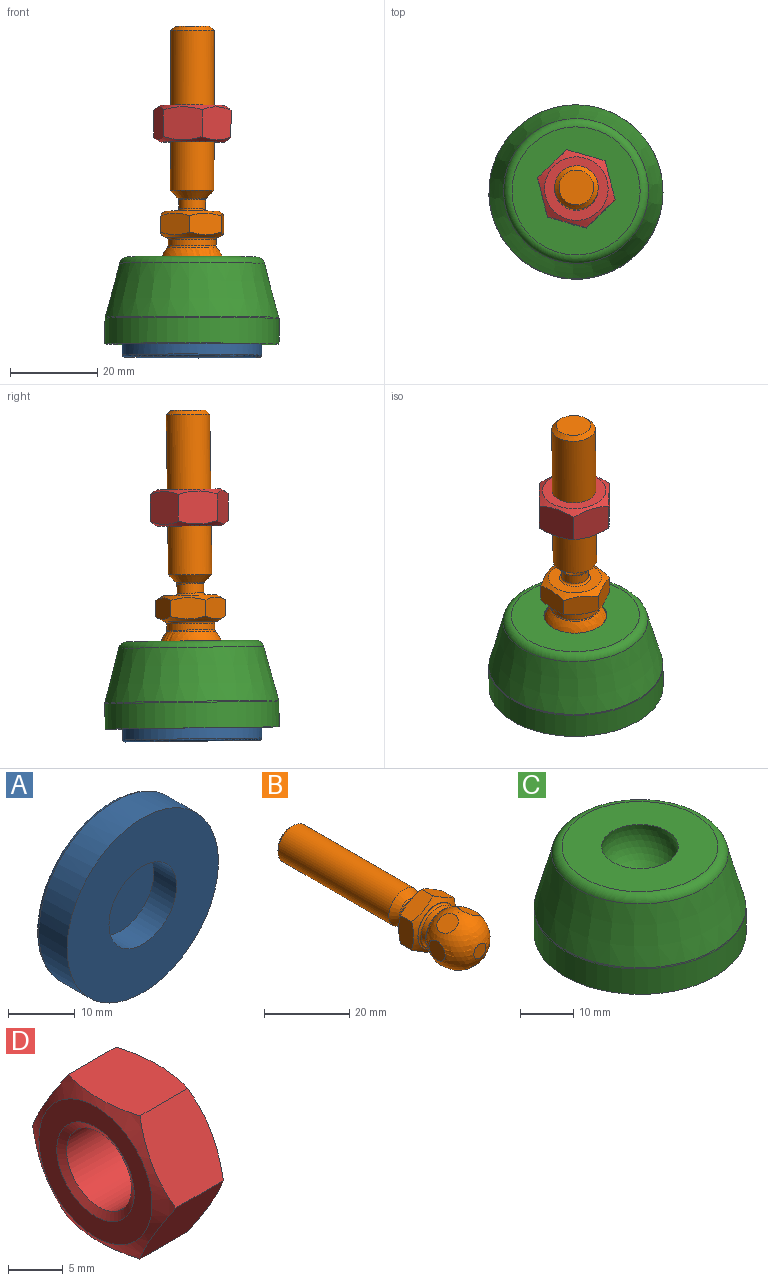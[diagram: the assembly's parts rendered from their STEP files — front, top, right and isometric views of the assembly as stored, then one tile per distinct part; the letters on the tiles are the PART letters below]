
ASSEMBLY  parts=4 mates=3
PART A: 6 faces, bbox 34.6x6.5x34.6 mm
  f0: torus R=15.5mm, axis (0,1,0), area 78.1mm2, adj f1,f2
  f1: plane 31x31mm, normal (0,1,0), area 754.8mm2, adj f0
  f2: cylinder r=16mm len=32mm, axis (0,1,0), area 603.2mm2, adj f0,f5
  f3: plane 14.3x14.3mm, normal (0,-1,0), area 160.6mm2, adj f4
  f4: cylinder r=7.15mm len=14.3mm, axis (0,1,0), area 215.6mm2, adj f3,f5
  f5: plane 32x32mm, normal (0,-1,0), area 643.6mm2, adj f2,f4
PART B: 28 faces, bbox 16.2x63.3x16.2 mm
  f0: torus R=3.56mm, axis (0,-1,0), area 16mm2, adj f1,f2
  f1: cylinder r=3.06mm len=6.12mm, axis (0,1,0), area 40.2mm2, adj f0,f3
  f2: plane 12.17x12.17mm, normal (0,1,0), area 76.4mm2, adj f0,f11
  f3: torus R=3.56mm, axis (0,1,0), area 7.7mm2, adj f1,f4
  f4: cone r=4.03mm half-angle=45deg, axis (0,1,0), area 65.4mm2, adj f3,f16
  f5: torus R=6mm, axis (0,1,0), area 12.6mm2, adj f6,f7
  f6: cylinder r=5.5mm len=11mm, axis (0,1,0), area 51.1mm2, adj f5,f8
  f7: sphere r=7.5mm, area 433mm2, adj f5,f18,f19,f20,f21,f22,f23,f27
  f8: torus R=6mm, axis (0,1,0), area 28mm2, adj f6,f9
  f9: plane 12.17x12.17mm, normal (0,-1,0), area 3.1mm2, adj f8,f10
  f10: cone r=7.08mm half-angle=60deg, axis (0,1,0), area 61.8mm2, adj f9,f12,f13,f14,f24,f25,f26
  f11: cone r=7.08mm half-angle=60deg, axis (0,-1,0), area 61.8mm2, adj f2,f12,f13,f14,f24,f25,f26
  f12: plane 7x5.54mm, normal (-0.5,0,-0.87), area 36.5mm2, adj f10,f11,f13,f25
  f13: plane 8.08x5.54mm, normal (-1,0,0), area 36.5mm2, adj f10,f11,f12,f14
  f14: plane 7x5.54mm, normal (-0.5,0,0.87), area 36.5mm2, adj f10,f11,f13,f24
  f15: cone r=4.5mm half-angle=45deg, axis (0,-1,0), area 40mm2, adj f16,f17
  f16: cylinder r=5mm len=36.76mm, axis (0,1,0), area 1154.8mm2, adj f4,f15
  f17: plane 8x8mm, normal (0,1,0), area 50.3mm2, adj f15
  f18: plane 5.39x5.39mm, normal (-1,0,0), area 22.8mm2, adj f7
  f19: plane 5.39x4.66mm, normal (-0.5,0,-0.87), area 22.8mm2, adj f7
  f20: plane 5.39x4.66mm, normal (0.5,0,-0.87), area 22.8mm2, adj f7
  f21: plane 5.39x5.39mm, normal (1,0,0), area 22.8mm2, adj f7
  f22: plane 5.39x4.66mm, normal (0.5,0,0.87), area 22.8mm2, adj f7
  f23: plane 5.39x4.66mm, normal (-0.5,0,0.87), area 22.8mm2, adj f7
  f24: plane 7x5.54mm, normal (0.5,0,0.87), area 36.5mm2, adj f10,f11,f14,f26
  f25: plane 7x5.54mm, normal (0.5,0,-0.87), area 36.5mm2, adj f10,f11,f12,f26
  f26: plane 8.08x5.54mm, normal (1,0,0), area 36.5mm2, adj f10,f11,f24,f25
  f27: plane 4x4mm, normal (0,-1,0), area 12.6mm2, adj f7
PART C: 58 faces, bbox 43.3x43.3x20 mm
  f0: plane 9x6.43mm, normal (0.71,-0.71,0), area 69.3mm2, adj f2,f27,f35,f43,f45,f56
  f1: plane 9x6.43mm, normal (-0.71,0.71,0), area 69.3mm2, adj f2,f28,f36,f44,f45,f56
  f2: plane 8.55x8.55mm, normal (0,0,-1), area 27.1mm2, adj f0,f1,f45,f56
  f3: plane 9.09x9mm, normal (0,-1,0), area 69.3mm2, adj f5,f28,f36,f44,f45,f56
  f4: plane 9.09x9mm, normal (0,1,0), area 69.3mm2, adj f5,f26,f34,f42,f45,f56
  f5: plane 9.16x3mm, normal (0,0,-1), area 27.1mm2, adj f3,f4,f45,f56
  f6: plane 9x6.43mm, normal (-0.71,-0.71,0), area 69.3mm2, adj f8,f26,f34,f42,f45,f56
  f7: plane 9x6.43mm, normal (0.71,0.71,0), area 69.3mm2, adj f8,f25,f33,f41,f45,f56
  f8: plane 8.55x8.55mm, normal (0,0,-1), area 27.1mm2, adj f6,f7,f45,f56
  f9: plane 9.09x9mm, normal (-1,0,0), area 69.3mm2, adj f11,f25,f33,f41,f45,f56
  f10: plane 9.09x9mm, normal (1,0,0), area 69.3mm2, adj f11,f24,f32,f40,f45,f56
  f11: plane 9.16x3mm, normal (0,0,-1), area 27.1mm2, adj f9,f10,f45,f56
  f12: plane 9x6.43mm, normal (-0.71,0.71,0), area 69.3mm2, adj f14,f24,f32,f40,f45,f56
  f13: plane 9x6.43mm, normal (0.71,-0.71,0), area 69.3mm2, adj f14,f23,f31,f39,f45,f56
  f14: plane 8.55x8.55mm, normal (0,0,-1), area 27.1mm2, adj f12,f13,f45,f56
  f15: plane 9.09x9mm, normal (0,1,0), area 69.3mm2, adj f17,f23,f31,f39,f45,f56
  f16: plane 9.09x9mm, normal (0,-1,0), area 69.3mm2, adj f17,f22,f30,f38,f45,f56
  f17: plane 9.16x3mm, normal (0,0,-1), area 27.1mm2, adj f15,f16,f45,f56
  f18: plane 9x6.43mm, normal (0.71,0.71,0), area 69.3mm2, adj f20,f22,f30,f38,f45,f56
  f19: plane 9x6.43mm, normal (-0.71,-0.71,0), area 69.3mm2, adj f20,f21,f29,f37,f45,f56
  f20: plane 8.55x8.55mm, normal (0,0,-1), area 27.1mm2, adj f18,f19,f45,f56
  f21: sphere r=10mm, area 13.1mm2, adj f19,f29,f47,f56
  f22: sphere r=10mm, area 13.1mm2, adj f16,f18,f30,f56
  f23: sphere r=10mm, area 13.1mm2, adj f13,f15,f31,f56
  f24: sphere r=10mm, area 13.1mm2, adj f10,f12,f32,f56
  f25: sphere r=10mm, area 13.1mm2, adj f7,f9,f33,f56
  f26: sphere r=10mm, area 13.1mm2, adj f4,f6,f34,f56
  f27: sphere r=10mm, area 13.1mm2, adj f0,f35,f46,f56
  f28: sphere r=10mm, area 13.1mm2, adj f1,f3,f36,f56
  f29: plane 7.18x6.32mm, normal (0,0,-1), area 28.3mm2, adj f19,f21,f37,f47
  f30: plane 7.18x6.32mm, normal (0,0,-1), area 28.3mm2, adj f16,f18,f22,f38
  f31: plane 7.18x6.32mm, normal (0,0,-1), area 28.3mm2, adj f13,f15,f23,f39
  f32: plane 7.18x6.32mm, normal (0,0,-1), area 28.3mm2, adj f10,f12,f24,f40
  f33: plane 7.18x6.32mm, normal (0,0,-1), area 28.3mm2, adj f7,f9,f25,f41
  f34: plane 7.18x6.32mm, normal (0,0,-1), area 28.3mm2, adj f4,f6,f26,f42
  f35: plane 7.18x6.32mm, normal (0,0,-1), area 28.3mm2, adj f0,f27,f43,f46
  f36: plane 7.18x6.32mm, normal (0,0,-1), area 28.3mm2, adj f1,f3,f28,f44
  f37: cone r=14.93mm half-angle=15deg, axis (0,0,-1), area 72.2mm2, adj f19,f29,f45,f47
  f38: cone r=14.93mm half-angle=15deg, axis (0,0,-1), area 72.2mm2, adj f16,f18,f30,f45
  f39: cone r=14.93mm half-angle=15deg, axis (0,0,-1), area 72.2mm2, adj f13,f15,f31,f45
  f40: cone r=14.93mm half-angle=15deg, axis (0,0,-1), area 72.2mm2, adj f10,f12,f32,f45
  f41: cone r=14.93mm half-angle=15deg, axis (0,0,-1), area 72.2mm2, adj f7,f9,f33,f45
  f42: cone r=14.93mm half-angle=15deg, axis (0,0,-1), area 72.2mm2, adj f4,f6,f34,f45
  f43: cone r=14.93mm half-angle=15deg, axis (0,0,-1), area 72.2mm2, adj f0,f35,f45,f46
  f44: cone r=14.93mm half-angle=15deg, axis (0,0,-1), area 72.2mm2, adj f1,f3,f36,f45
  f45: cylinder r=16mm len=32mm, axis (0,0,1), area 579.2mm2, adj f0,f1,f2,f3,f4,f5,f6,f7
  f46: plane 9.09x9mm, normal (-1,0,0), area 69.3mm2, adj f27,f35,f43,f45,f48,f56
  f47: plane 9.09x9mm, normal (1,0,0), area 69.3mm2, adj f21,f29,f37,f45,f48,f56
  f48: plane 9.16x3mm, normal (0,0,-1), area 27.1mm2, adj f45,f46,f47,f56
  f49: plane 14x14mm, normal (0,0,-1), area 153.9mm2, adj f56
  f50: torus R=19mm, axis (0,0,-1), area 32.9mm2, adj f51,f52
  f51: cone r=20mm half-angle=15deg, axis (0,0,-1), area 1475.4mm2, adj f50,f53
  f52: cylinder r=20mm len=40mm, axis (0,0,1), area 737.4mm2, adj f50,f57
  f53: torus R=14.71mm, axis (0,0,-1), area 260.7mm2, adj f51,f54
  f54: plane 29.43x29.43mm, normal (0,0,1), area 516mm2, adj f53,f55
  f55: sphere r=7.5mm, area 447.7mm2, adj f54
  f56: cylinder r=7mm len=14mm, axis (0,0,1), area 291.9mm2, adj f0,f1,f2,f3,f4,f5,f6,f7
  f57: plane 40x40mm, normal (0,0,-1), area 452.4mm2, adj f45,f52
PART D: 13 faces, bbox 8.4x18.5x18.5 mm
  f0: cone r=4.59mm half-angle=60deg, axis (-1,0,0), area 27.1mm2, adj f1,f2
  f1: cylinder r=4.19mm len=8.38mm, axis (1,0,0), area 196.4mm2, adj f0,f3
  f2: plane 14.6x14.6mm, normal (-1,0,0), area 88.9mm2, adj f0,f5
  f3: cone r=4.59mm half-angle=60deg, axis (1,0,0), area 27.1mm2, adj f1,f4
  f4: plane 14.6x14.6mm, normal (1,0,0), area 88.9mm2, adj f3,f6
  f5: cone r=8.27mm half-angle=60deg, axis (1,0,0), area 62.7mm2, adj f2,f7,f8,f9,f10,f11,f12
  f6: cone r=8.27mm half-angle=60deg, axis (-1,0,0), area 62.7mm2, adj f4,f7,f8,f9,f10,f11,f12
  f7: plane 8.27x8mm, normal (0,0.87,-0.5), area 65.6mm2, adj f5,f6,f8,f9
  f8: plane 9.24x8.27mm, normal (0,0,-1), area 65.6mm2, adj f5,f6,f7,f11
  f9: plane 8.27x8mm, normal (0,0.87,0.5), area 65.6mm2, adj f5,f6,f7,f10
  f10: plane 9.24x8.27mm, normal (0,0,1), area 65.6mm2, adj f5,f6,f9,f12
  f11: plane 8.27x8mm, normal (0,-0.87,-0.5), area 65.6mm2, adj f5,f6,f8,f12
  f12: plane 8.27x8mm, normal (0,-0.87,0.5), area 65.6mm2, adj f5,f6,f10,f11
PLACE A rot(axis=(-0.75,0.47,-0.47),107deg) t=(71.43,-20.25,-50.7)mm
PLACE B rot(axis=(0.75,-0.47,-0.47),105.8deg) t=(71.47,-19.97,-29.7)mm
PLACE C rot(axis=(0,0.01,1),115.8deg) t=(71.42,-20.29,-54.2)mm
PLACE D rot(axis=(0.36,0.86,-0.37),98.6deg) t=(71.52,-19.56,0.62)mm
MATE fastened A.f0 <-> C.f37  axis (0,-0.01,-1) through (71.42,-20.33,-57.2)mm
MATE fastened C.f37 <-> B.f5  axis (0,0.01,1) through (71.46,-20.03,-34.2)mm
MATE cylindrical B.f16 <-> D.f0  axis (0,0.01,1) through (71.52,-19.58,-0.58)mm
